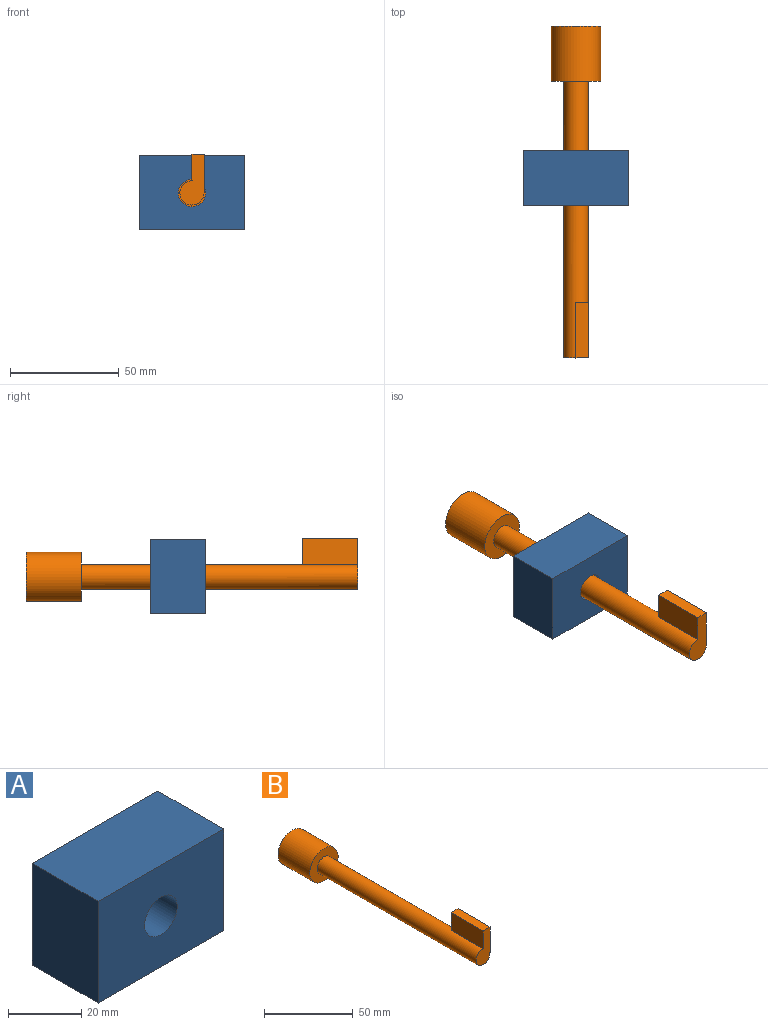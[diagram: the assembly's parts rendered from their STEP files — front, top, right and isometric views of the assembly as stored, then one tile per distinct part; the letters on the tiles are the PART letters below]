
ASSEMBLY  parts=2 mates=1
PART A: 7 faces, bbox 48.4x25.4x34 mm
  f0: plane 33.99x25.4mm, normal (-1,0,0), area 863.3mm2, adj f1,f4,f5,f6
  f1: plane 48.43x25.4mm, normal (0,0,-1), area 1230mm2, adj f0,f2,f5,f6
  f2: plane 33.99x25.4mm, normal (1,0,0), area 863.3mm2, adj f1,f4,f5,f6
  f3: cylinder r=6.28mm len=25.4mm, axis (0,1,0), area 1002.9mm2, adj f5,f6
  f4: plane 48.43x25.4mm, normal (0,0,1), area 1230mm2, adj f0,f2,f5,f6
  f5: plane 48.43x33.99mm, normal (0,-1,0), area 1521.9mm2, adj f0,f1,f2,f3,f4
  f6: plane 48.43x33.99mm, normal (0,1,0), area 1521.9mm2, adj f0,f1,f2,f3,f4
PART B: 10 faces, bbox 22.6x152.4x29.1 mm
  f0: cylinder r=5.55mm len=127mm, axis (0,1,0), area 4205.2mm2, adj f1,f2,f3,f6,f9
  f1: plane 23.4x11.11mm, normal (0,-1,0), area 171.9mm2, adj f0,f2,f3,f4,f5
  f2: plane 25.4x12.31mm, normal (-1,0,0), area 312.6mm2, adj f0,f1,f5,f6
  f3: plane 25.4x0.02mm, normal (0,0,-1), area 0.4mm2, adj f0,f1,f4,f6
  f4: plane 25.4x17.86mm, normal (1,0,0), area 453.5mm2, adj f1,f3,f5,f6
  f5: plane 25.4x5.56mm, normal (0,0,1), area 141.3mm2, adj f1,f2,f4,f6
  f6: plane 17.86x5.56mm, normal (0,1,0), area 75.2mm2, adj f0,f2,f3,f4,f5
  f7: cylinder r=11.28mm len=25.4mm, axis (0,-1,0), area 1800.4mm2, adj f8,f9
  f8: plane 22.56x22.56mm, normal (0,1,0), area 399.8mm2, adj f7
  f9: plane 22.56x22.56mm, normal (0,-1,0), area 303.1mm2, adj f0,f7
PLACE A rot(axis=(0,-1,0),0deg) t=(-81.02,17.38,-194.23)mm fixed
PLACE B rot(axis=(0,-1,0),0deg) t=(-123.13,49.13,-223.75)mm
MATE cylindrical B.f0 <-> A.f3  axis (0,1,0) through (-81.02,49.13,-194.23)mm
